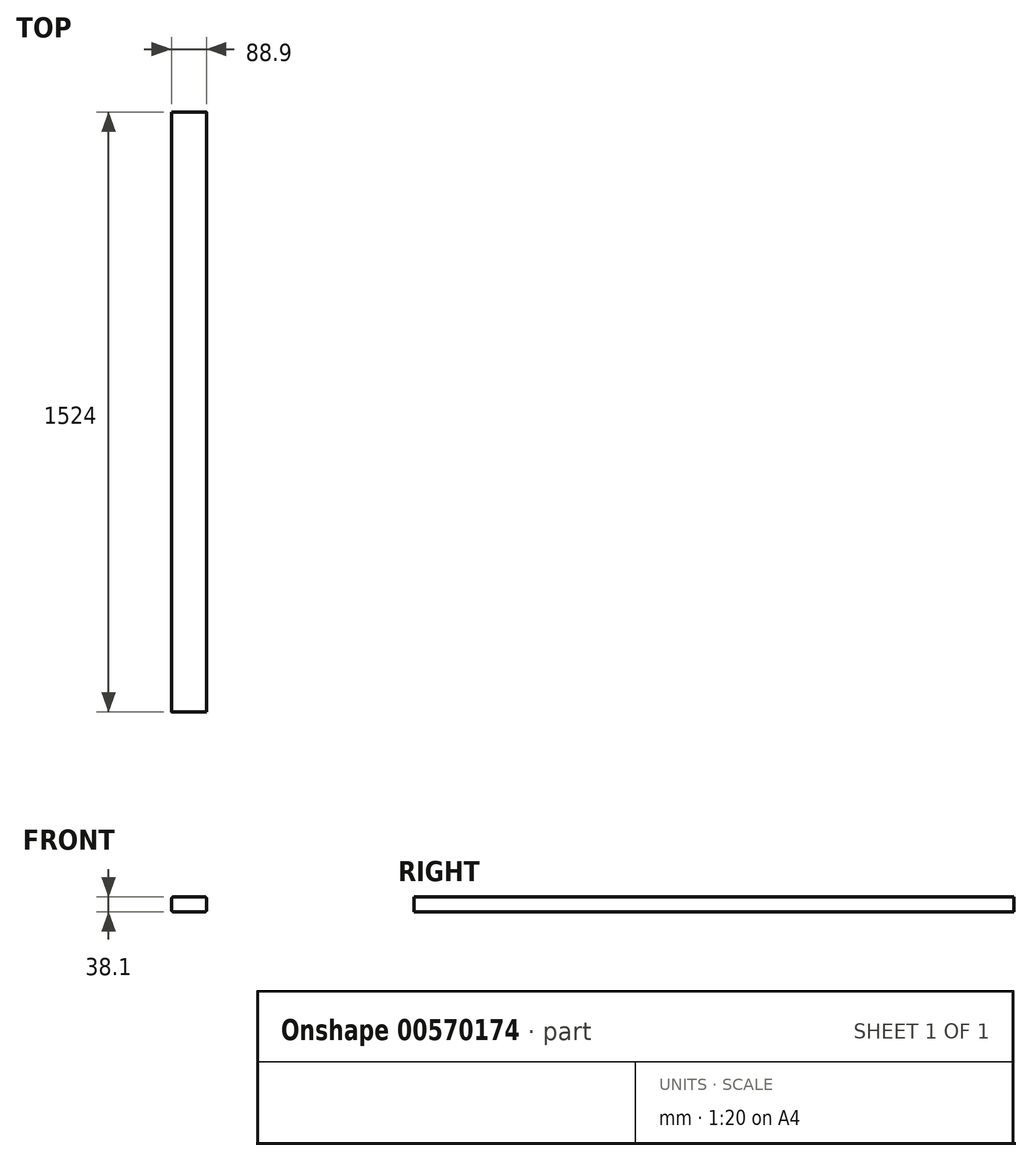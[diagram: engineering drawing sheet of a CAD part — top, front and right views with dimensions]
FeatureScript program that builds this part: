
annotation { "Feature Type Name" : "Feature", "Feature Type Description" : "" }
export const myFeature = defineFeature(function(context is Context, id is Id, definition is map)
    precondition{}
    {
        {
            var Q0;
            Q0=qCreatedBy(makeId("Front.planeOp"),FACE);
            var sketch = newSketch(context, id + "F0", { "sketchPlane" : qUnion([Q0])});
            skLineSegment(sketch, "E0.bottom", {"start": v(0, 0) * mm, "end": v(88.9, 0) * mm});
            skLineSegment(sketch, "E0.top", {"start": v(0, 38.1) * mm, "end": v(88.9, 38.1) * mm});
            skLineSegment(sketch, "E0.left", {"start": v(0, 0) * mm, "end": v(0, 38.1) * mm});
            skLineSegment(sketch, "E0.right", {"start": v(88.9, 0) * mm, "end": v(88.9, 38.1) * mm});
            skSolve(sketch);
        }
        {
            var Q0;
            Q0 = qSketchRegion(id + "F0", true);
            extrude(context, id + "F1", {"entities" : qUnion([Q0]), "depth" : 1524 * mm, "offsetDistance" : 25.4 * mm});
        }
        {
            var Q0;
            Q0=makeQuery(id+"F1.opExtrude","SWEPT_EDGE",EDGE,{"disambiguationData":[OSD([sQuery(id+"F0.wireOp",EDGE,"E0.top"),sQuery(id+"F0.wireOp",EDGE,"E0.left")])]});
            var Q1;
            Q1=makeQuery(id+"F1.opExtrude","SWEPT_EDGE",EDGE,{"disambiguationData":[OSD([sQuery(id+"F0.wireOp",EDGE,"E0.top"),sQuery(id+"F0.wireOp",EDGE,"E0.right")])]});
            var Q2;
            Q2=makeQuery(id+"F1.opExtrude","SWEPT_EDGE",EDGE,{"disambiguationData":[OSD([sQuery(id+"F0.wireOp",EDGE,"E0.bottom"),sQuery(id+"F0.wireOp",EDGE,"E0.right")])]});
            var Q3;
            Q3=makeQuery(id+"F1.opExtrude","SWEPT_EDGE",EDGE,{"disambiguationData":[OSD([sQuery(id+"F0.wireOp",EDGE,"E0.bottom"),sQuery(id+"F0.wireOp",EDGE,"E0.left")])]});
            fillet(context, id + "F2", {"entities" : qUnion([Q0, Q1, Q2, Q3]), "radius" : 5.08 * mm, "tangentPropagation" : true, "allowEdgeOverflow" : false});
        }
    });
